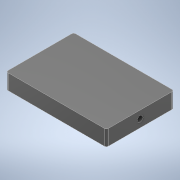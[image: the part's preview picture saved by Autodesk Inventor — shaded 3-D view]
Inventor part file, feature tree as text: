
AUTODESK INVENTOR PART (.ipt)
format: ipt  version: 2021 (Build 250183000, 183)  size: 120,832 bytes
history: native  units: mm
features: sketch x3, hole x2, other x1, extrude x1, fillet x1
ambient origin geometry x8: Origin, YZ Plane, XZ Plane, XY Plane, X Axis, Y Axis, Z Axis, Center Point
bodies: Body1 (feature_tree)
feature tree (8):
  other  "Sólido1"
  extrude  "Extrusão1"  Depth=35.0mm
  fillet  "Arredondamento1"  Radius=8.0mm
  hole  "Furo1"  [1 undecoded]
  hole  "Furo2"  [1 undecoded]
  sketch  "Esboço1"  dims[d0=52.0mm d1=35.0mm d2=8.0mm d3=0.0mm]
  sketch  "Esboço2"  dims[d4=1.0mm d5=4.0mm]
  sketch  "Esboço3"  dims[d6=3.0mm d7=6.0mm d8=4.0mm d9=2.0mm d10=90.0deg d11=5.0mm d12=20.594885mm d13=4.0mm d14=3.0mm d15=6.0mm d16=4.0mm d17=2.0mm d18=90.0deg d19=5.0mm d20=20.594885mm]
note: 2 required parameter values undecoded (feature->parameter linkage not recoverable at this tier; creation-order binding heuristic only, values carry confidence <= 0.55)
